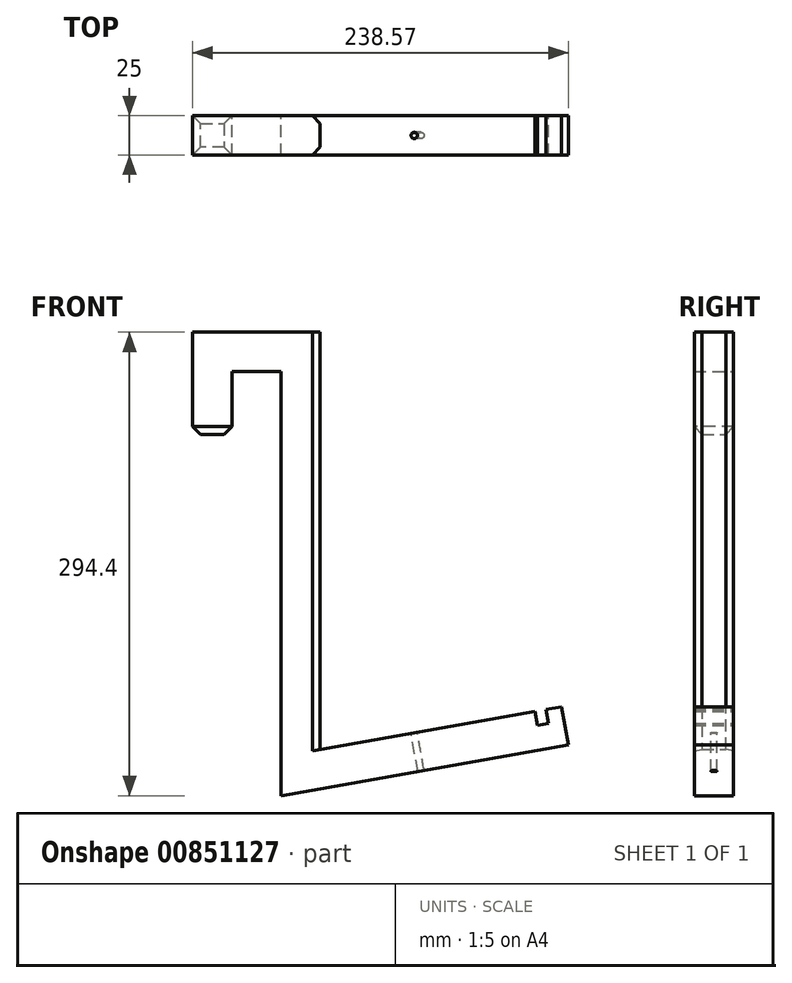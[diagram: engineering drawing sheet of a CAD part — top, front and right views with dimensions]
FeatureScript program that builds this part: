
annotation { "Feature Type Name" : "Feature", "Feature Type Description" : "" }
export const myFeature = defineFeature(function(context is Context, id is Id, definition is map)
    precondition{}
    {
        {
            var Q0;
            Q0=qCreatedBy(makeId("Front.planeOp"),FACE);
            var sketch = newSketch(context, id + "F0", { "sketchPlane" : qUnion([Q0])});
            skLineSegment(sketch, "E0", {"start": v(-56, 69.65) * mm, "end": v(-56, 134.65) * mm});
            skLineSegment(sketch, "E1", {"start": v(-56, 134.65) * mm, "end": v(25, 134.65) * mm});
            skLineSegment(sketch, "E2", {"start": v(25, 134.65) * mm, "end": v(25, -130.35) * mm});
            skLineSegment(sketch, "E3", {"start": v(25, -130.35) * mm, "end": v(161.55, -106.27) * mm});
            skLineSegment(sketch, "E4", {"start": v(178.3, -103.32) * mm, "end": v(182.57, -127.56) * mm});
            skLineSegment(sketch, "E5", {"start": v(182.57, -127.56) * mm, "end": v(25, -155.35) * mm});
            skLineSegment(sketch, "E6", {"start": v(0, -155.35) * mm, "end": v(0, 109.65) * mm});
            skLineSegment(sketch, "E7", {"start": v(0, 109.65) * mm, "end": v(-31, 109.65) * mm});
            skLineSegment(sketch, "E8", {"start": v(-31, 109.65) * mm, "end": v(-31, 69.65) * mm});
            skLineSegment(sketch, "E9", {"start": v(-31, 69.65) * mm, "end": v(-56, 69.65) * mm});
            skLineSegment(sketch, "E10", {"start": v(168.45, -105.05) * mm, "end": v(170, -113.92) * mm});
            skLineSegment(sketch, "E11", {"start": v(170, -113.92) * mm, "end": v(163.12, -115.13) * mm});
            skLineSegment(sketch, "E12", {"start": v(163.12, -115.13) * mm, "end": v(161.55, -106.27) * mm});
            skLineSegment(sketch, "E13.trimOffspring", {"start": v(168.45, -105.05) * mm, "end": v(178.3, -103.32) * mm});
            skLineSegment(sketch, "E14", {"start": v(25, -155.35) * mm, "end": v(0, -159.75) * mm});
            skLineSegment(sketch, "E15", {"start": v(0, -155.35) * mm, "end": v(0, -159.75) * mm});
            skSolve(sketch);
        }
        {
            var Q0;
            Q0 = qSketchRegion(id + "F0", true);
            extrude(context, id + "F1", {"entities" : qUnion([Q0]), "depth" : 25 * mm, "offsetDistance" : 25 * mm});
        }
        {
            var Q0;
            Q0=makeQuery(id+"F1.opExtrude","SWEPT_FACE",FACE,{"disambiguationData":[OSD([sQuery(id+"F0.wireOp",EDGE,"E3")])]});
            var sketch = newSketch(context, id + "F2", { "sketchPlane" : qUnion([Q0])});
            skCircle(sketch, "E16", {"center": v(62.64, -12.5) * mm, "radius": 2 * mm});
            skSolve(sketch);
        }
        {
            var Q0;
            Q0 = qSketchRegion(id + "F2", true);
            extrude(context, id + "F3", {"entities" : qUnion([Q0]), "operationType" : NewBodyOperationType.REMOVE, "oppositeDirection" : true, "depth" : 27 * mm, "offsetDistance" : 25 * mm});
        }
        {
            var Q0;
            Q0=makeQuery(id+"F1.opExtrude","CAP_EDGE",EDGE,{"disambiguationData":[OSD([sQuery(id+"F0.wireOp",EDGE,"E2")])],"isStart":false});
            var Q1;
            Q1=makeQuery(id+"F1.opExtrude","CAP_EDGE",EDGE,{"disambiguationData":[OSD([sQuery(id+"F0.wireOp",EDGE,"E2")])],"isStart":true});
            var Q2;
            Q2=makeQuery(id+"F1.opExtrude","CAP_EDGE",EDGE,{"disambiguationData":[OSD([sQuery(id+"F0.wireOp",EDGE,"E9")])],"isStart":false});
            var Q3;
            Q3=makeQuery(id+"F1.opExtrude","SWEPT_FACE",FACE,{"disambiguationData":[OSD([sQuery(id+"F0.wireOp",EDGE,"E9")])]});
            chamfer(context, id + "F4", {"entities" : qUnion([Q0, Q1, Q2, Q3]), "width" : 5 * mm, "tangentPropagation" : true});
        }
    });
